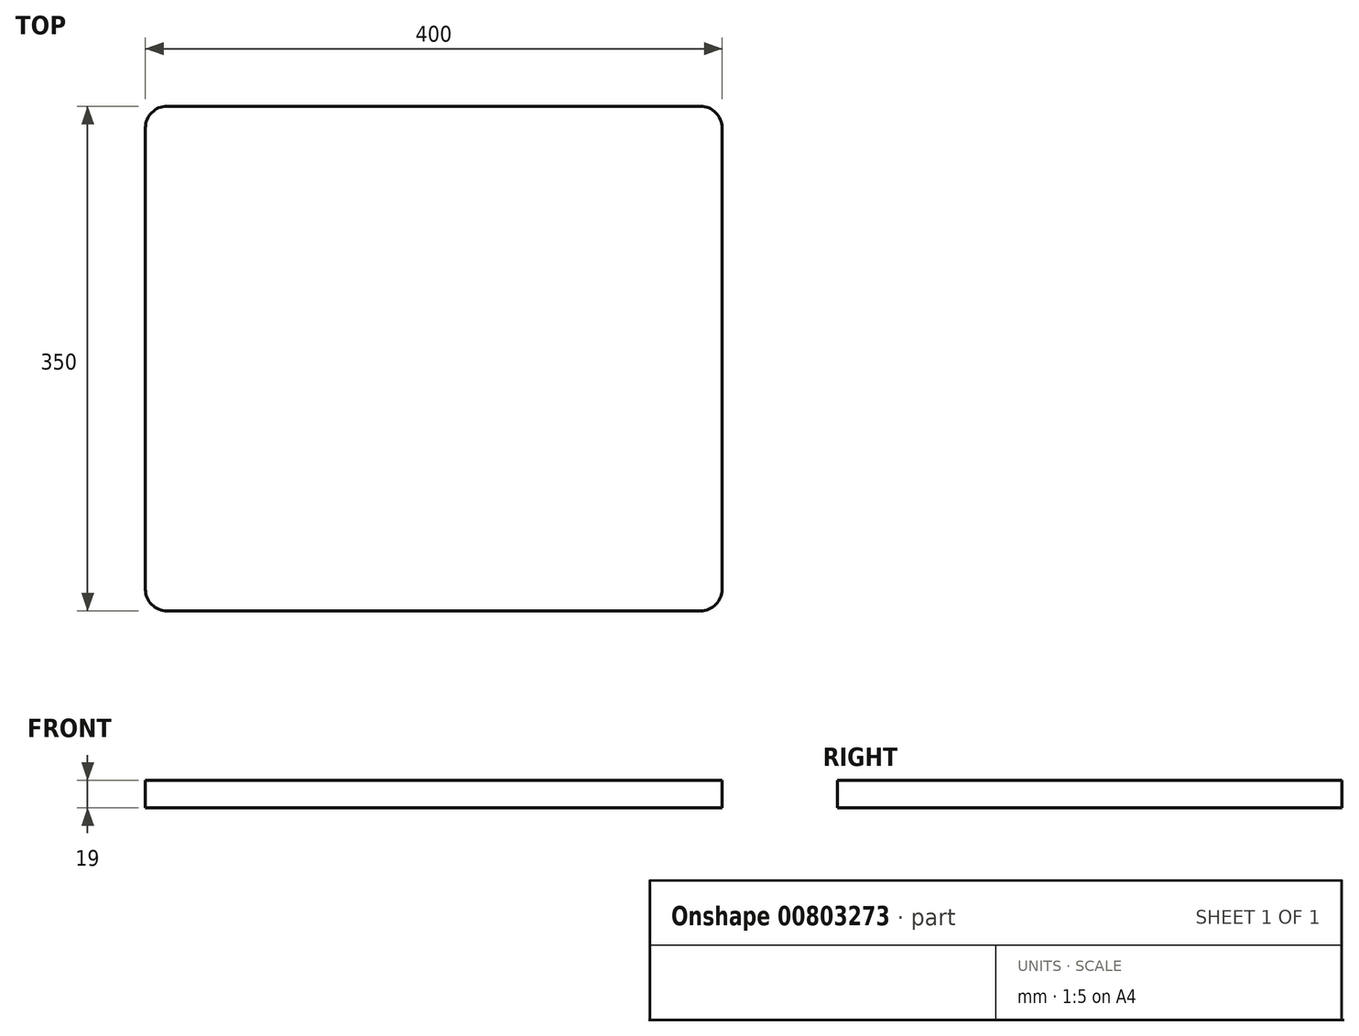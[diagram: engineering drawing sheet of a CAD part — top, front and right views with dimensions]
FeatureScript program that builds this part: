
annotation { "Feature Type Name" : "Feature", "Feature Type Description" : "" }
export const myFeature = defineFeature(function(context is Context, id is Id, definition is map)
    precondition{}
    {
        {
            var Q0;
            Q0=qCreatedBy(makeId("Top.planeOp"),FACE);
            var sketch = newSketch(context, id + "F0", { "sketchPlane" : qUnion([Q0])});
            skLineSegment(sketch, "E0.bottom", {"start": v(-269.9, 0) * mm, "end": v(100.1, 0) * mm});
            skLineSegment(sketch, "E0.top", {"start": v(-269.9, -350) * mm, "end": v(100.1, -350) * mm});
            skLineSegment(sketch, "E0.left", {"start": v(-284.9, -15) * mm, "end": v(-284.9, -335) * mm});
            skLineSegment(sketch, "E0.right", {"start": v(115.1, -15) * mm, "end": v(115.1, -335) * mm});
            skPoint(sketch, "E1.visualSharp", {"position": v(-284.9, 0) * mm});
            skArc(sketch, "E1.filletArc", {"start": v(-269.9, 0) * mm, "mid": v(-280.51, -4.4) * mm, "end": v(-284.9, -15) * mm});
            skPoint(sketch, "E2.visualSharp", {"position": v(115.1, 0) * mm});
            skArc(sketch, "E2.filletArc", {"start": v(115.1, -15) * mm, "mid": v(110.7, -4.4) * mm, "end": v(100.1, 0) * mm});
            skPoint(sketch, "E3.visualSharp", {"position": v(115.1, -350) * mm});
            skArc(sketch, "E3.filletArc", {"start": v(100.1, -350) * mm, "mid": v(110.7, -345.6) * mm, "end": v(115.1, -335) * mm});
            skPoint(sketch, "E4.visualSharp", {"position": v(-284.9, -350) * mm});
            skArc(sketch, "E4.filletArc", {"start": v(-284.9, -335) * mm, "mid": v(-280.51, -345.6) * mm, "end": v(-269.9, -350) * mm});
            skSolve(sketch);
        }
        {
            var Q0;
            Q0=makeQuery(id+"F0.imprint","IMPRINT",FACE,{"disambiguationData":[TD([[makeQuery(id+"F0.imprint","IMPRINT",EDGE,{"derivedFrom":sQuery(id+"F0.wireOp",EDGE,"E0.bottom")}),-1.0]])]});
            extrude(context, id + "F1", {"entities" : qUnion([Q0]), "depth" : 19 * mm, "offsetDistance" : 25 * mm});
        }
    });
